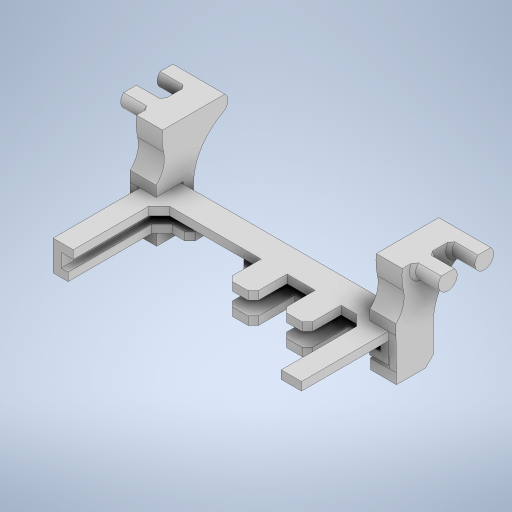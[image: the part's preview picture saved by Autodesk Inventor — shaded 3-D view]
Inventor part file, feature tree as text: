
AUTODESK INVENTOR PART (.ipt)
format: ipt  version: 2024.3 (Build 283343000, 343)  size: 549,888 bytes
history: native  units: mm
features: extrude x10, sketch x8, other x8, reference x7, projected_geometry x6, chamfer x4, plane x1, mirror x1
ambient origin geometry x8: Origin, YZ Plane, XZ Plane, XY Plane, X Axis, Y Axis, Z Axis, Center Point
bodies: Solid1 (feature_tree), Solid2 (feature_tree), Solid3 (feature_tree)
feature tree (45):
  extrude  "Extrusion1"  Depth=0.3mm
  extrude  "Extrusion2"  Depth=1.0mm
  sketch  "Sketch3"  dims[d5=0.3mm d6=1.0mm]
  extrude  "Extrusion3"  Depth=1.0mm
  extrude  "Extrusion4"  Depth=2.0mm
  chamfer  "Chamfer1"  Distance=3.5mm
  extrude  "Extrusion5"  Depth=2.0mm TaperAngle=45.0deg
  extrude  "Extrusion6"  Depth=1.0mm
  chamfer  "Chamfer2"  Distance=15.0mm
  plane  "Work Plane1"
  extrude  "Extrusion7"  Depth=0.5mm
  extrude  "Extrusion8"  Depth=1.4mm
  chamfer  "Chamfer3"  Distance=8.0mm
  extrude  "Extrusion9"  Depth=1.0mm TaperAngle=45.0deg
  chamfer  "Chamfer4"  Distance=0.2mm
  extrude  "Extrusion10"  Depth=0.2mm
  mirror  "Mirror1"
  sketch  "Sketch1"  dims[d0=1.5mm d1=0.0mm d2=0.3mm]
  reference  "Reference1"
  reference  "Reference2"
  sketch  "Sketch2"  dims[d3=1.6mm d4=1.0mm]
  reference  "Reference3"
  reference  "Reference4"
  projected_geometry  "Projected Loop1"
  projected_geometry  "Projected Loop2"
  sketch  "Sketch4"  dims[d7=20.0mm d8=0.0mm d9=2.0mm d10=3.5mm d11=0.0mm]
  reference  "Reference5"
  reference  "Reference6"
  projected_geometry  "Projected Loop3"
  sketch  "Sketch5"  dims[d12=2.0mm d13=0.0mm d14=2.0mm d15=2.0mm d16=45.0deg]
  reference  "Reference7"
  sketch  "Sketch6"  dims[d17=1.0mm d18=1.0mm d19=15.0mm d20=0.0mm]
  sketch  "Sketch7"  dims[d21=0.5mm d22=0.5mm]
  projected_geometry  "Projected Loop6"
  projected_geometry  "Projected Loop7"
  sketch  "Sketch8"  dims[d23=0.5mm d24=0.5mm d25=8.0mm d26=0.0mm d27=1.0mm d28=2.0mm d29=45.0deg d30=0.2mm d31=0.2mm d32=0.2mm d33=5.0mm d34=5.0mm d35=0.0mm d36=0.0mm d37=60.0deg d38=12.0mm d39=5.0mm d40=0.0mm d41=0.6mm d42=2.0mm d43=45.0deg d44=0.2mm d46=2.0mm d47=5.0mm d48=10.0mm d49=5.0mm d50=0.0mm d51=1.5mm d52=2.0mm d53=45.0deg d54=1.4mm d55=0.0mm]
  projected_geometry  "Projected Loop8"
  other  "Pattern of Solid2:1"
  other  "<userpath> TUF\Documents\Inventor\ParkinsonDetection\Prototy-1.iam"
  other  "Prototy-1.iam"
  other  "PCB-V1:1"
  other  "Switch:1"
  other  "Socket:2"
  other  "Socket:1"
  other  "Case-Bottom:1"
